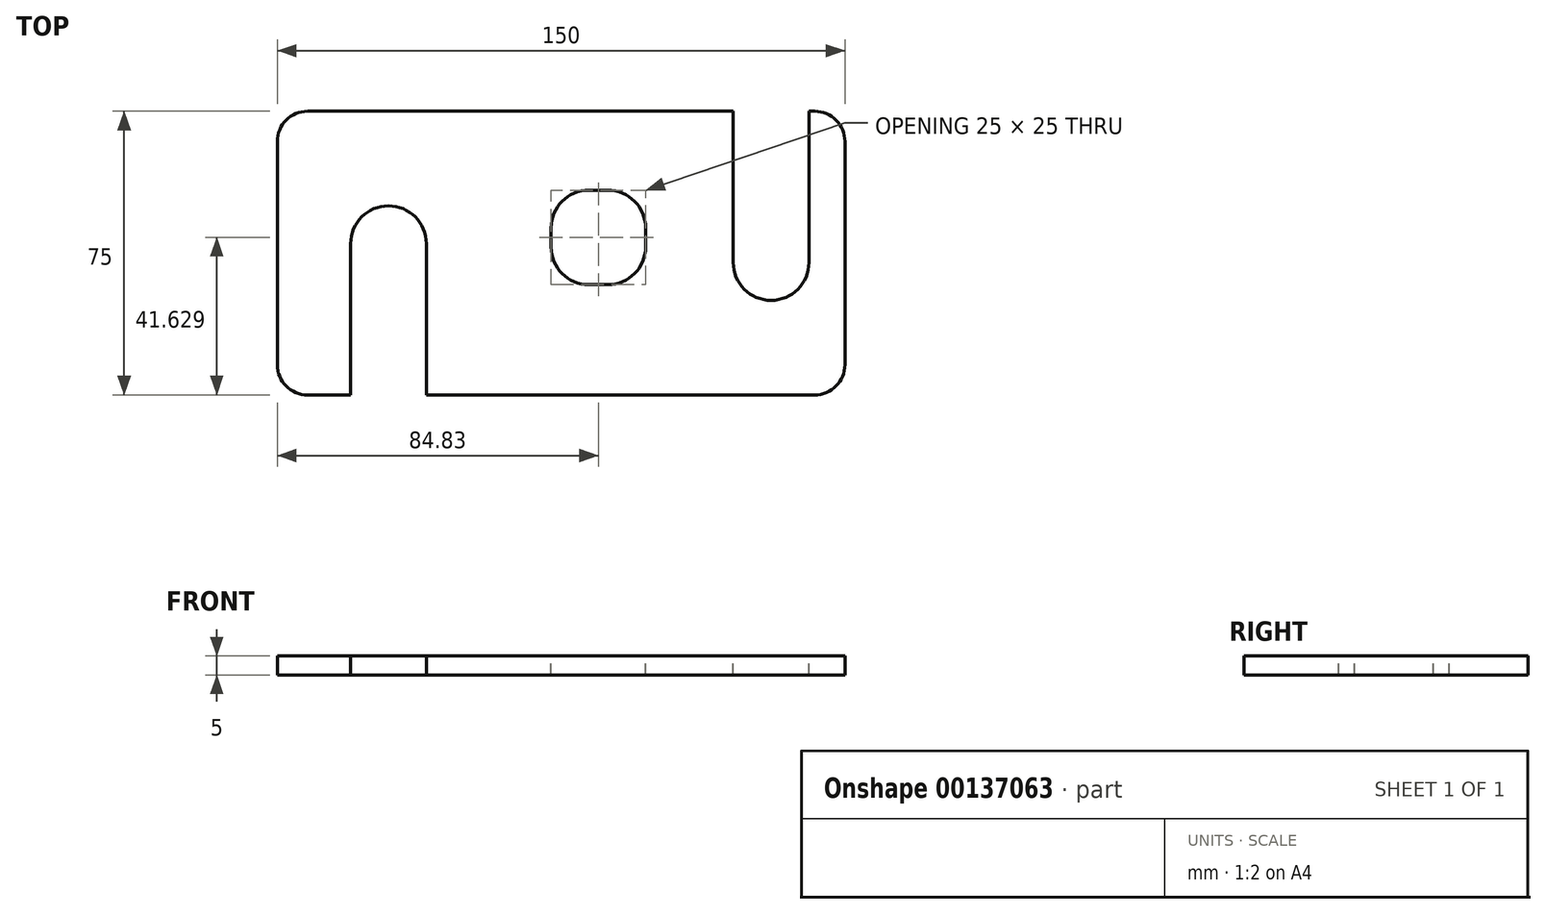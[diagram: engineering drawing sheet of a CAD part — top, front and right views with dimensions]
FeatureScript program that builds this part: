
annotation { "Feature Type Name" : "Feature", "Feature Type Description" : "" }
export const myFeature = defineFeature(function(context is Context, id is Id, definition is map)
    precondition{}
    {
        {
            var Q0;
            Q0=qCreatedBy(makeId("Top.planeOp"),FACE);
            var sketch = newSketch(context, id + "F0", { "sketchPlane" : qUnion([Q0])});
            skLineSegment(sketch, "E0.bottom", {"start": v(-109.16, 38.33) * mm, "end": v(40.84, 38.33) * mm});
            skLineSegment(sketch, "E0.top", {"start": v(-109.16, -36.67) * mm, "end": v(40.84, -36.67) * mm});
            skLineSegment(sketch, "E0.left", {"start": v(-109.16, 38.33) * mm, "end": v(-109.16, -36.67) * mm});
            skLineSegment(sketch, "E0.right", {"start": v(40.84, 38.33) * mm, "end": v(40.84, -36.67) * mm});
            skSolve(sketch);
        }
        {
            var Q0;
            Q0 = qSketchRegion(id + "F0", true);
            extrude(context, id + "F1", {"entities" : qUnion([Q0]), "depth" : 5 * mm});
        }
        {
            var Q0;
            Q0=makeQuery(id+"F1.opExtrude","CAP_FACE",FACE,{"disambiguationData":[OSD([sQuery(id+"F0.wireOp",EDGE,"E0.bottom"),sQuery(id+"F0.wireOp",EDGE,"E0.top"),sQuery(id+"F0.wireOp",EDGE,"E0.left"),sQuery(id+"F0.wireOp",EDGE,"E0.right")])],"isStart":false});
            var sketch = newSketch(context, id + "F2", { "sketchPlane" : qUnion([Q0])});
            skLineSegment(sketch, "E1", {"start": v(-89.78, -36.67) * mm, "end": v(-89.78, 3.33) * mm});
            skLineSegment(sketch, "E2", {"start": v(-69.78, -36.67) * mm, "end": v(-69.78, 3.33) * mm});
            skLineSegment(sketch, "E3", {"start": v(-89.78, -36.67) * mm, "end": v(-69.78, -36.67) * mm});
            skArc(sketch, "E4", {"start": v(-69.78, 3.33) * mm, "mid": v(-79.78, 13.33) * mm, "end": v(-89.78, 3.33) * mm});
            skSolve(sketch);
        }
        {
            var Q0;
            Q0 = qSketchRegion(id + "F2", true);
            extrude(context, id + "F3", {"entities" : qUnion([Q0]), "operationType" : NewBodyOperationType.REMOVE, "endBound" : BoundingType.THROUGH_ALL, "oppositeDirection" : true, "depth" : 25 * mm});
        }
        {
            var Q0;
            Q0=makeQuery(id+"F1.opExtrude","CAP_FACE",FACE,{"disambiguationData":[OSD([sQuery(id+"F0.wireOp",EDGE,"E0.bottom"),sQuery(id+"F0.wireOp",EDGE,"E0.top"),sQuery(id+"F0.wireOp",EDGE,"E0.left"),sQuery(id+"F0.wireOp",EDGE,"E0.right")])],"isStart":false});
            var sketch = newSketch(context, id + "F4", { "sketchPlane" : qUnion([Q0])});
            skLineSegment(sketch, "E5", {"start": v(31.32, 38.33) * mm, "end": v(31.32, -1.67) * mm});
            skLineSegment(sketch, "E6", {"start": v(11.32, 38.33) * mm, "end": v(11.32, -1.67) * mm});
            skLineSegment(sketch, "E7", {"start": v(11.32, 38.33) * mm, "end": v(31.32, 38.33) * mm});
            skArc(sketch, "E8", {"start": v(31.32, -1.67) * mm, "mid": v(21.32, -11.67) * mm, "end": v(11.32, -1.67) * mm});
            skSolve(sketch);
        }
        {
            var Q0;
            Q0 = qSketchRegion(id + "F4", true);
            extrude(context, id + "F5", {"entities" : qUnion([Q0]), "operationType" : NewBodyOperationType.REMOVE, "endBound" : BoundingType.THROUGH_ALL, "oppositeDirection" : true, "depth" : 25 * mm});
        }
        {
            var Q0;
            Q0=makeQuery(id+"F1.opExtrude","CAP_FACE",FACE,{"disambiguationData":[OSD([sQuery(id+"F0.wireOp",EDGE,"E0.bottom"),sQuery(id+"F0.wireOp",EDGE,"E0.top"),sQuery(id+"F0.wireOp",EDGE,"E0.left"),sQuery(id+"F0.wireOp",EDGE,"E0.right")])],"isStart":false});
            var sketch = newSketch(context, id + "F6", { "sketchPlane" : qUnion([Q0])});
            skLineSegment(sketch, "E9.bottom", {"start": v(-36.83, 17.46) * mm, "end": v(-11.83, 17.46) * mm});
            skLineSegment(sketch, "E9.top", {"start": v(-36.83, -7.54) * mm, "end": v(-11.83, -7.54) * mm});
            skLineSegment(sketch, "E9.left", {"start": v(-36.83, 17.46) * mm, "end": v(-36.83, -7.54) * mm});
            skLineSegment(sketch, "E9.right", {"start": v(-11.83, 17.46) * mm, "end": v(-11.83, -7.54) * mm});
            skSolve(sketch);
        }
        {
            var Q0;
            Q0 = qSketchRegion(id + "F6", true);
            extrude(context, id + "F7", {"entities" : qUnion([Q0]), "operationType" : NewBodyOperationType.REMOVE, "endBound" : BoundingType.THROUGH_ALL, "oppositeDirection" : true, "depth" : 25 * mm});
        }
        {
            var Q0;
            Q0=makeQuery(id+"F7.boolean.opBoolean","COPY",EDGE,{"derivedFrom":makeQuery(id+"F7.opExtrude","SWEPT_EDGE",EDGE,{"disambiguationData":[OSD([sQuery(id+"F6.wireOp",EDGE,"E9.top"),sQuery(id+"F6.wireOp",EDGE,"E9.left")])]})});
            var Q1;
            Q1=makeQuery(id+"F7.boolean.opBoolean","COPY",EDGE,{"derivedFrom":makeQuery(id+"F7.opExtrude","SWEPT_EDGE",EDGE,{"disambiguationData":[OSD([sQuery(id+"F6.wireOp",EDGE,"E9.top"),sQuery(id+"F6.wireOp",EDGE,"E9.right")])]})});
            var Q2;
            Q2=makeQuery(id+"F7.boolean.opBoolean","COPY",EDGE,{"derivedFrom":makeQuery(id+"F7.opExtrude","SWEPT_EDGE",EDGE,{"disambiguationData":[OSD([sQuery(id+"F6.wireOp",EDGE,"E9.bottom"),sQuery(id+"F6.wireOp",EDGE,"E9.right")])]})});
            var Q3;
            Q3=makeQuery(id+"F7.boolean.opBoolean","COPY",EDGE,{"derivedFrom":makeQuery(id+"F7.opExtrude","SWEPT_EDGE",EDGE,{"disambiguationData":[OSD([sQuery(id+"F6.wireOp",EDGE,"E9.bottom"),sQuery(id+"F6.wireOp",EDGE,"E9.left")])]})});
            fillet(context, id + "F8", {"entities" : qUnion([Q0, Q1, Q2, Q3]), "radius" : 10 * mm, "tangentPropagation" : true, "allowEdgeOverflow" : false});
        }
        {
            var Q0;
            Q0=makeQuery(id+"F1.opExtrude","SWEPT_EDGE",EDGE,{"disambiguationData":[OSD([sQuery(id+"F0.wireOp",EDGE,"E0.bottom"),sQuery(id+"F0.wireOp",EDGE,"E0.right")])]});
            var Q1;
            Q1=makeQuery(id+"F1.opExtrude","SWEPT_EDGE",EDGE,{"disambiguationData":[OSD([sQuery(id+"F0.wireOp",EDGE,"E0.top"),sQuery(id+"F0.wireOp",EDGE,"E0.left")])]});
            var Q2;
            Q2=makeQuery(id+"F1.opExtrude","SWEPT_EDGE",EDGE,{"disambiguationData":[OSD([sQuery(id+"F0.wireOp",EDGE,"E0.top"),sQuery(id+"F0.wireOp",EDGE,"E0.right")])]});
            var Q3;
            Q3=makeQuery(id+"F1.opExtrude","SWEPT_EDGE",EDGE,{"disambiguationData":[OSD([sQuery(id+"F0.wireOp",EDGE,"E0.bottom"),sQuery(id+"F0.wireOp",EDGE,"E0.left")])]});
            fillet(context, id + "F9", {"entities" : qUnion([Q0, Q1, Q2, Q3]), "radius" : 8 * mm, "tangentPropagation" : true, "allowEdgeOverflow" : false});
        }
    });
